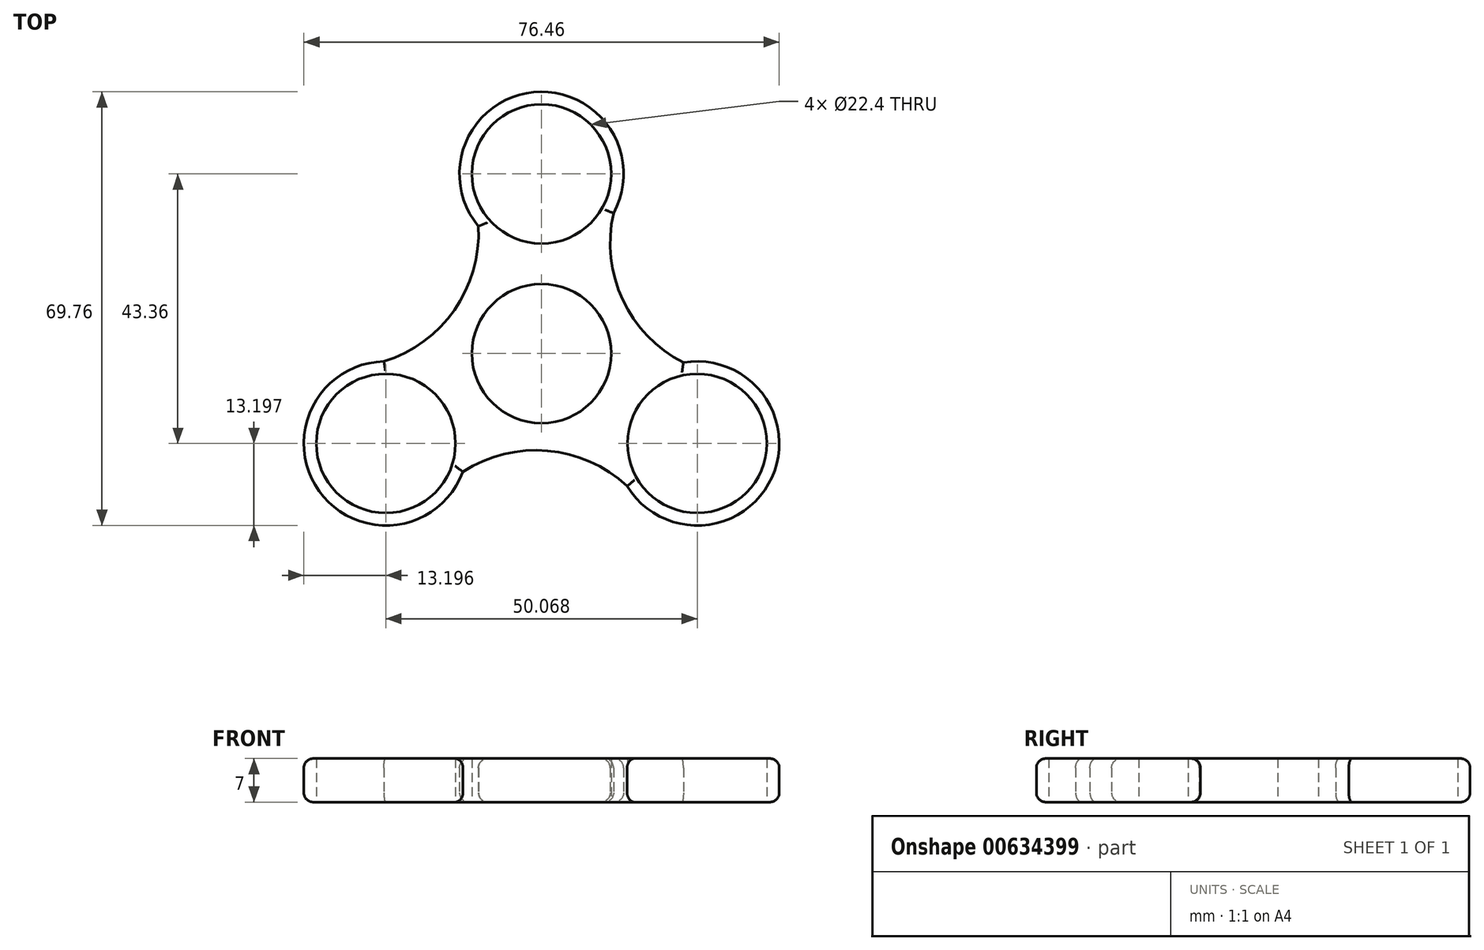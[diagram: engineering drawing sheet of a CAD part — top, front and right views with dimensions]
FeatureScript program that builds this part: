
annotation { "Feature Type Name" : "Feature", "Feature Type Description" : "" }
export const myFeature = defineFeature(function(context is Context, id is Id, definition is map)
    precondition{}
    {
        {
            var Q0;
            Q0=qCreatedBy(makeId("Top.planeOp"),FACE);
            var sketch = newSketch(context, id + "F0", { "sketchPlane" : qUnion([Q0])});
            skCircle(sketch, "E0", {"center": v(0, 0) * mm, "radius": 11.2 * mm});
            skCircle(sketch, "E1", {"center": v(0, 28.9) * mm, "radius": 11.2 * mm});
            skArc(sketch, "E2", {"start": v(11.59, 22.59) * mm, "mid": v(-1.27, 42.05) * mm, "end": v(-10.16, 20.48) * mm});
            skArc(sketch, "E3.1.0", {"start": v(-25.36, -1.26) * mm, "mid": v(-35.78, -22.12) * mm, "end": v(-12.66, -19.04) * mm});
            skCircle(sketch, "E3.1.1", {"center": v(-25.03, -14.45) * mm, "radius": 11.2 * mm});
            skArc(sketch, "E3.2.0", {"start": v(13.77, -21.33) * mm, "mid": v(37.05, -19.92) * mm, "end": v(22.82, -1.44) * mm});
            skCircle(sketch, "E3.2.1", {"center": v(25.03, -14.45) * mm, "radius": 11.2 * mm});
            skArc(sketch, "E4", {"start": v(11.59, 22.59) * mm, "mid": v(13.07, 8.64) * mm, "end": v(22.82, -1.44) * mm});
            skArc(sketch, "E5.1.0", {"start": v(-25.36, -1.26) * mm, "mid": v(-14.02, 7) * mm, "end": v(-10.16, 20.48) * mm});
            skArc(sketch, "E5.2.0", {"start": v(13.77, -21.33) * mm, "mid": v(0.95, -15.64) * mm, "end": v(-12.66, -19.04) * mm});
            skSolve(sketch);
        }
        {
            var Q0;
            Q0=makeQuery(id+"F0.imprint","IMPRINT",FACE,{"disambiguationData":[TD([[makeQuery(id+"F0.imprint","IMPRINT",EDGE,{"derivedFrom":sQuery(id+"F0.wireOp",EDGE,"E0")}),-1.0]])]});
            extrude(context, id + "F1", {"entities" : qUnion([Q0]), "depth" : 7 * mm, "offsetDistance" : 25 * mm});
        }
        {
            var Q0;
            Q0=makeQuery(id+"F1.opExtrude","CAP_EDGE",EDGE,{"disambiguationData":[OSD([sQuery(id+"F0.wireOp",EDGE,"E4")])],"isStart":false});
            var Q1;
            Q1=makeQuery(id+"F1.opExtrude","CAP_EDGE",EDGE,{"disambiguationData":[OSD([sQuery(id+"F0.wireOp",EDGE,"E3.2.0")])],"isStart":false});
            var Q2;
            Q2=makeQuery(id+"F1.opExtrude","CAP_EDGE",EDGE,{"disambiguationData":[OSD([sQuery(id+"F0.wireOp",EDGE,"E5.2.0")])],"isStart":false});
            var Q3;
            Q3=makeQuery(id+"F1.opExtrude","CAP_EDGE",EDGE,{"disambiguationData":[OSD([sQuery(id+"F0.wireOp",EDGE,"E3.1.0")])],"isStart":false});
            var Q4;
            Q4=makeQuery(id+"F1.opExtrude","CAP_EDGE",EDGE,{"disambiguationData":[OSD([sQuery(id+"F0.wireOp",EDGE,"E5.1.0")])],"isStart":false});
            var Q5;
            Q5=makeQuery(id+"F1.opExtrude","CAP_EDGE",EDGE,{"disambiguationData":[OSD([sQuery(id+"F0.wireOp",EDGE,"E2")])],"isStart":false});
            var Q6;
            Q6=makeQuery(id+"F1.opExtrude","CAP_EDGE",EDGE,{"disambiguationData":[OSD([sQuery(id+"F0.wireOp",EDGE,"E4")])],"isStart":true});
            var Q7;
            Q7=makeQuery(id+"F1.opExtrude","CAP_EDGE",EDGE,{"disambiguationData":[OSD([sQuery(id+"F0.wireOp",EDGE,"E3.2.0")])],"isStart":true});
            var Q8;
            Q8=makeQuery(id+"F1.opExtrude","CAP_EDGE",EDGE,{"disambiguationData":[OSD([sQuery(id+"F0.wireOp",EDGE,"E2")])],"isStart":true});
            var Q9;
            Q9=makeQuery(id+"F1.opExtrude","CAP_EDGE",EDGE,{"disambiguationData":[OSD([sQuery(id+"F0.wireOp",EDGE,"E5.2.0")])],"isStart":true});
            var Q10;
            Q10=makeQuery(id+"F1.opExtrude","CAP_EDGE",EDGE,{"disambiguationData":[OSD([sQuery(id+"F0.wireOp",EDGE,"E3.1.0")])],"isStart":true});
            var Q11;
            Q11=makeQuery(id+"F1.opExtrude","CAP_EDGE",EDGE,{"disambiguationData":[OSD([sQuery(id+"F0.wireOp",EDGE,"E5.1.0")])],"isStart":true});
            fillet(context, id + "F2", {"entities" : qUnion([Q0, Q1, Q2, Q3, Q4, Q5, Q6, Q7, Q8, Q9, Q10, Q11]), "radius" : 1.5 * mm, "tangentPropagation" : true, "allowEdgeOverflow" : false});
        }
    });
